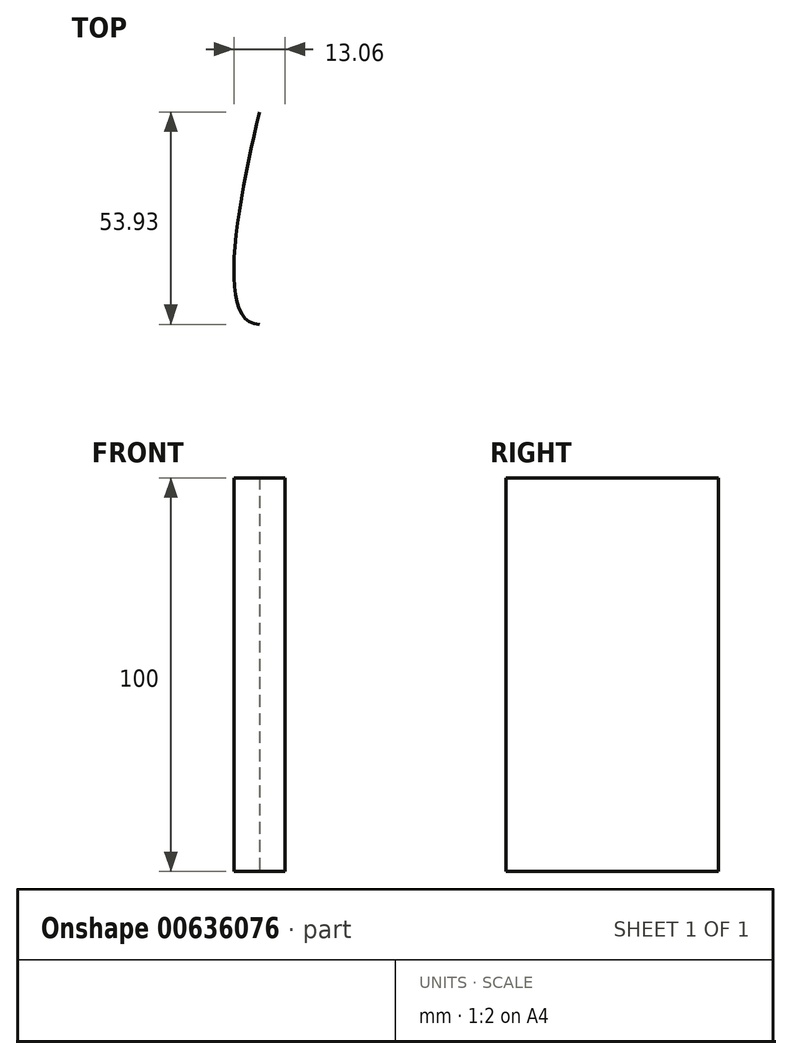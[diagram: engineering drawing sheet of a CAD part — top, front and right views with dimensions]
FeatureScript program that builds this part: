
annotation { "Feature Type Name" : "Feature", "Feature Type Description" : "" }
export const myFeature = defineFeature(function(context is Context, id is Id, definition is map)
    precondition{}
    {
        {
            var Q0;
            Q0=qCreatedBy(makeId("Top.planeOp"),FACE);
            var sketch = newSketch(context, id + "F0", { "sketchPlane" : qUnion([Q0])});
            skFitSpline(sketch, "E0", {"points": [v(0, 0) * mm, v(0, 53.93) * mm], "startDerivative": vector(34.46, 0) * mm, "endDerivative": vector(-16.23, 68.43) * mm});
            skFitSpline(sketch, "E1.MirrorCS", {"points": [v(0, 0) * mm, v(0, 53.93) * mm], "startDerivative": vector(-34.46, 0) * mm, "endDerivative": vector(16.23, 68.43) * mm});
            skSolve(sketch);
        }
        {
            var Q0;
            Q0 = qSketchRegion(id + "F0", true);
            extrude(context, id + "F1", {"entities" : qUnion([Q0]), "depth" : 100 * mm, "offsetDistance" : 25 * mm});
        }
    });
